# Revit family: Shelf-Metal-Caroma Cosmo
name_source: partatom
category: Specialty Equipment
revit_build: Autodesk Revit 2014 (Build: 20131024_2115(x64)
units: mm (PartAtom-declared; Revit-internal decimal feet)

## types (1)
- Standard
    Assembly Code = C1030200
    Cost = 0 $
    Default Elevation = 900 mm  [stored 2.95276 ft]
    Description = Contemporary style doesn't have to mean edges and angles with the Caroma Cosmo Accessory range
    Glazing = Glass-Clear-Caroma
    Height_ANZRS = 45 mm  [stored 0.147638 ft]
    Length_ANZRS = 380 mm
    Manufacturer = GWA Bathrooms & Kitchens
    Material_ANZRS = Metal-Chrome-Caroma
    Model = 305006C
    ModifiedIssue_ANZRS = 20150505.01 $
    Type Comments = Caroma Cosmo Metal Shelf
    URL = http://specify.caroma.com.au
    Width_ANZRS = 146 mm  [stored 0.479003 ft]

note: [stored X ft] marks values corroborated as IEEE doubles in the binary element streams (Revit-internal decimal feet)

## geometry (parser evidence)
native form markers: Blend x8, Sweep x1
no freeform markers — native parametric forms only
